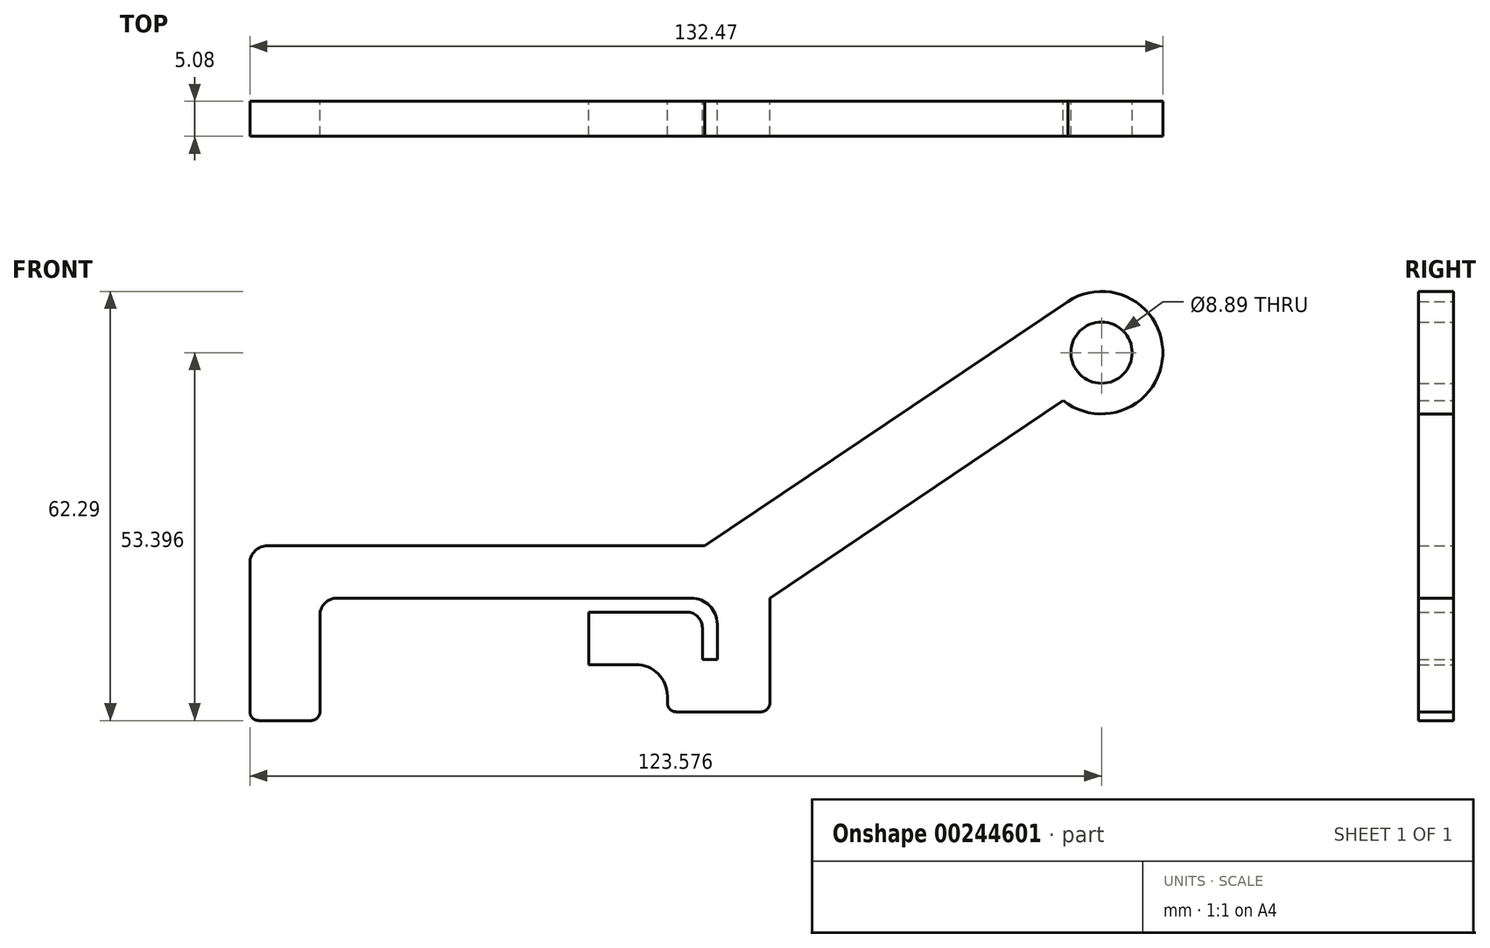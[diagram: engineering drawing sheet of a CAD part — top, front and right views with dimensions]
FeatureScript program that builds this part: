
annotation { "Feature Type Name" : "Feature", "Feature Type Description" : "" }
export const myFeature = defineFeature(function(context is Context, id is Id, definition is map)
    precondition{}
    {
        {
            var Q0;
            Q0=qCreatedBy(makeId("Front.planeOp"),FACE);
            var sketch = newSketch(context, id + "F0", { "sketchPlane" : qUnion([Q0])});
            skLineSegment(sketch, "E0", {"start": v(-18.6, 0) * mm, "end": v(32.7, 0) * mm});
            skLineSegment(sketch, "E1", {"start": v(36.52, -3.8) * mm, "end": v(36.52, -8.9) * mm});
            skLineSegment(sketch, "E2", {"start": v(36.52, -8.9) * mm, "end": v(34.36, -8.9) * mm});
            skLineSegment(sketch, "E3", {"start": v(30.55, -16.51) * mm, "end": v(42.87, -16.51) * mm});
            skLineSegment(sketch, "E4", {"start": v(44.14, -15.24) * mm, "end": v(44.14, 0) * mm});
            skLineSegment(sketch, "E5", {"start": v(-31.3, 0) * mm, "end": v(-31.3, -16.51) * mm});
            skLineSegment(sketch, "E6", {"start": v(-30.03, -17.78) * mm, "end": v(-22.41, -17.78) * mm});
            skLineSegment(sketch, "E7", {"start": v(-21.14, -16.51) * mm, "end": v(-21.14, -2.54) * mm});
            skLineSegment(sketch, "E8", {"start": v(29.28, -15.24) * mm, "end": v(29.28, -14.22) * mm});
            skLineSegment(sketch, "E9", {"start": v(29.28, -2.03) * mm, "end": v(32.07, -2.03) * mm});
            skLineSegment(sketch, "E10", {"start": v(34.36, -4.32) * mm, "end": v(34.36, -8.9) * mm});
            skPoint(sketch, "E11.visualSharp", {"position": v(36.52, 0) * mm});
            skArc(sketch, "E11.filletArc", {"start": v(36.52, -3.8) * mm, "mid": v(35.4, -1.12) * mm, "end": v(32.7, 0) * mm});
            skPoint(sketch, "E12.visualSharp", {"position": v(-21.14, 0) * mm});
            skArc(sketch, "E12.filletArc", {"start": v(-18.6, 0) * mm, "mid": v(-20.4, -0.74) * mm, "end": v(-21.14, -2.54) * mm});
            skLineSegment(sketch, "E13", {"start": v(29.28, -2.03) * mm, "end": v(17.85, -2.03) * mm});
            skLineSegment(sketch, "E14", {"start": v(17.85, -2.03) * mm, "end": v(17.85, -9.65) * mm});
            skLineSegment(sketch, "E15", {"start": v(17.85, -9.65) * mm, "end": v(24.7, -9.65) * mm});
            skPoint(sketch, "E16.visualSharp", {"position": v(34.36, -2.03) * mm});
            skArc(sketch, "E16.filletArc", {"start": v(34.36, -4.32) * mm, "mid": v(33.69, -2.7) * mm, "end": v(32.07, -2.03) * mm});
            skPoint(sketch, "E17.visualSharp", {"position": v(29.28, -9.65) * mm});
            skArc(sketch, "E17.filletArc", {"start": v(29.28, -14.22) * mm, "mid": v(27.94, -11) * mm, "end": v(24.7, -9.65) * mm});
            skPoint(sketch, "E18.visualSharp", {"position": v(29.28, -16.51) * mm});
            skArc(sketch, "E18.filletArc", {"start": v(29.28, -15.24) * mm, "mid": v(29.65, -16.14) * mm, "end": v(30.55, -16.51) * mm});
            skPoint(sketch, "E19.visualSharp", {"position": v(44.14, -16.5) * mm});
            skArc(sketch, "E19.filletArc", {"start": v(42.87, -16.5) * mm, "mid": v(43.76, -16.14) * mm, "end": v(44.14, -15.24) * mm});
            skPoint(sketch, "E20.visualSharp", {"position": v(-21.14, -17.78) * mm});
            skArc(sketch, "E20.filletArc", {"start": v(-22.41, -17.78) * mm, "mid": v(-21.51, -17.4) * mm, "end": v(-21.14, -16.51) * mm});
            skPoint(sketch, "E21.visualSharp", {"position": v(-31.3, -17.78) * mm});
            skArc(sketch, "E21.filletArc", {"start": v(-31.3, -16.51) * mm, "mid": v(-30.93, -17.4) * mm, "end": v(-30.03, -17.78) * mm});
            skLineSegment(sketch, "E22", {"start": v(-31.3, 0) * mm, "end": v(-31.3, 5.05) * mm});
            skLineSegment(sketch, "E23", {"start": v(-28.76, 7.6) * mm, "end": v(34.7, 7.6) * mm});
            skLineSegment(sketch, "E24", {"start": v(34.7, 7.6) * mm, "end": v(87.39, 43.04) * mm});
            skArc(sketch, "E25", {"start": v(86.73, 28.67) * mm, "mid": v(101.16, 35.21) * mm, "end": v(87.39, 43.04) * mm});
            skLineSegment(sketch, "E26", {"start": v(44.14, 0) * mm, "end": v(86.73, 28.67) * mm});
            skCircle(sketch, "E27", {"center": v(92.28, 35.62) * mm, "radius": 4.45 * mm});
            skPoint(sketch, "E28.visualSharp", {"position": v(-31.3, 7.6) * mm});
            skArc(sketch, "E28.filletArc", {"start": v(-28.76, 7.6) * mm, "mid": v(-30.56, 6.85) * mm, "end": v(-31.3, 5.05) * mm});
            skSolve(sketch);
        }
        {
            var Q0;
            Q0=qSketchRegion(id+"F0",true);
            extrude(context, id + "F1", {"entities" : qUnion([Q0]), "depth" : 5.08 * mm});
        }
    });
